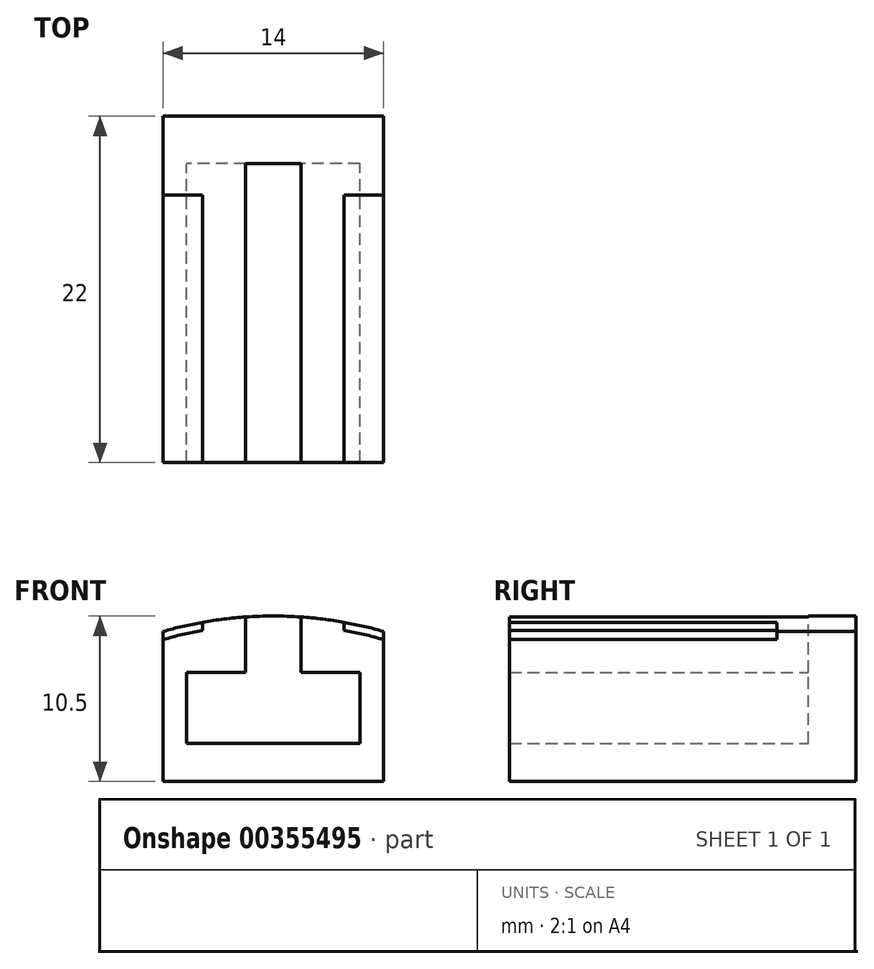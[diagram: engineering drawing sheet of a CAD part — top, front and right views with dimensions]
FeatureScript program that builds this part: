
annotation { "Feature Type Name" : "Feature", "Feature Type Description" : "" }
export const myFeature = defineFeature(function(context is Context, id is Id, definition is map)
    precondition{}
    {
        {
            var Q0;
            Q0=qCreatedBy(makeId("Front.planeOp"),FACE);
            var sketch = newSketch(context, id + "F0", { "sketchPlane" : qUnion([Q0])});
            skArc(sketch, "E0", {"start": v(7, 24.52) * mm, "mid": v(0, 25.5) * mm, "end": v(-7, 24.52) * mm});
            skLineSegment(sketch, "E1", {"start": v(0, 15) * mm, "end": v(-7.5, 15) * mm});
            skLineSegment(sketch, "E2", {"start": v(-2, 21.92) * mm, "end": v(-5.5, 21.92) * mm});
            skLineSegment(sketch, "E3.MirrorCS", {"start": v(2, 21.92) * mm, "end": v(5.5, 21.92) * mm});
            skLineSegment(sketch, "E4.MirrorCS", {"start": v(0, 15) * mm, "end": v(7, 15) * mm});
            skPoint(sketch, "E5.start.orphan", {"position": v(0, 25.5) * mm});
            skPoint(sketch, "E6.start.orphan", {"position": v(25.5, 0) * mm});
            skLineSegment(sketch, "E7", {"start": v(-7.5, 15) * mm, "end": v(-7, 15) * mm});
            skLineSegment(sketch, "E8", {"start": v(-7, 15) * mm, "end": v(-7, 24.52) * mm});
            skLineSegment(sketch, "E9.MirrorCS", {"start": v(7, 15) * mm, "end": v(7, 24.52) * mm});
            skArc(sketch, "E10", {"start": v(-4.5, 24.6) * mm, "mid": v(-5.76, 24.33) * mm, "end": v(-7, 24) * mm});
            skLineSegment(sketch, "E11", {"start": v(-4.5, 25.1) * mm, "end": v(-4.5, 24.6) * mm});
            skLineSegment(sketch, "E12.MirrorCS", {"start": v(4.5, 25.1) * mm, "end": v(4.5, 24.6) * mm});
            skArc(sketch, "E13.trimOffspring", {"start": v(7, 24) * mm, "mid": v(5.76, 24.33) * mm, "end": v(4.5, 24.6) * mm});
            skLineSegment(sketch, "E14", {"start": v(5.5, 17.42) * mm, "end": v(5.5, 21.92) * mm});
            skLineSegment(sketch, "E15.MirrorCS", {"start": v(-5.5, 17.42) * mm, "end": v(-5.5, 21.92) * mm});
            skLineSegment(sketch, "E16", {"start": v(2, 21.92) * mm, "end": v(1.75, 21.92) * mm});
            skLineSegment(sketch, "E17", {"start": v(1.75, 21.92) * mm, "end": v(1.75, 25.44) * mm});
            skLineSegment(sketch, "E18.MirrorCS", {"start": v(-1.75, 21.92) * mm, "end": v(-1.75, 25.44) * mm});
            skLineSegment(sketch, "E19.MirrorCS", {"start": v(-2, 21.92) * mm, "end": v(-1.75, 21.92) * mm});
            skLineSegment(sketch, "E20", {"start": v(0, 17.42) * mm, "end": v(5.5, 17.42) * mm});
            skLineSegment(sketch, "E21.MirrorCS", {"start": v(0, 17.42) * mm, "end": v(-5.5, 17.42) * mm});
            skSolve(sketch);
        }
        {
            var Q0;
            Q0=makeQuery(id+"F0.imprint","IMPRINT",FACE,{"disambiguationData":[TD([[makeQuery(id+"F0.imprint","IMPRINT",EDGE,{"derivedFrom":sQuery(id+"F0.wireOp",EDGE,"E1")}),-1.0]])]});
            extrude(context, id + "F1", {"entities" : qUnion([Q0]), "depth" : 22 * mm});
        }
        {
            var Q0;
            {var subQ4=sQuery(id+"F0.wireOp",EDGE,"E10");Q0=makeQuery(id+"F0.imprint","IMPRINT",FACE,{"disambiguationData":[TD([[makeQuery(id+"F0.imprint","IMPRINT",EDGE,{"derivedFrom":subQ4}),-1.0]])]});}
            extrude(context, id + "F2", {"entities" : qUnion([Q0]), "operationType" : NewBodyOperationType.ADD, "depth" : 5 * mm});
        }
        {
            var Q0;
            {var subQ3=sQuery(id+"F0.wireOp",EDGE,"E12.MirrorCS");Q0=makeQuery(id+"F0.imprint","IMPRINT",FACE,{"disambiguationData":[TD([[makeQuery(id+"F0.imprint","IMPRINT",EDGE,{"derivedFrom":subQ3}),1.0]])]});}
            extrude(context, id + "F3", {"entities" : qUnion([Q0]), "operationType" : NewBodyOperationType.ADD, "depth" : 5 * mm});
        }
        {
            var Q0;
            Q0=makeQuery(id+"F0.imprint","IMPRINT",FACE,{"disambiguationData":[TD([[makeQuery(id+"F0.imprint","IMPRINT",EDGE,{"derivedFrom":sQuery(id+"F0.wireOp",EDGE,"E2")}),1.0]])]});
            extrude(context, id + "F4", {"entities" : qUnion([Q0]), "operationType" : NewBodyOperationType.ADD, "depth" : 3 * mm});
        }
    });
